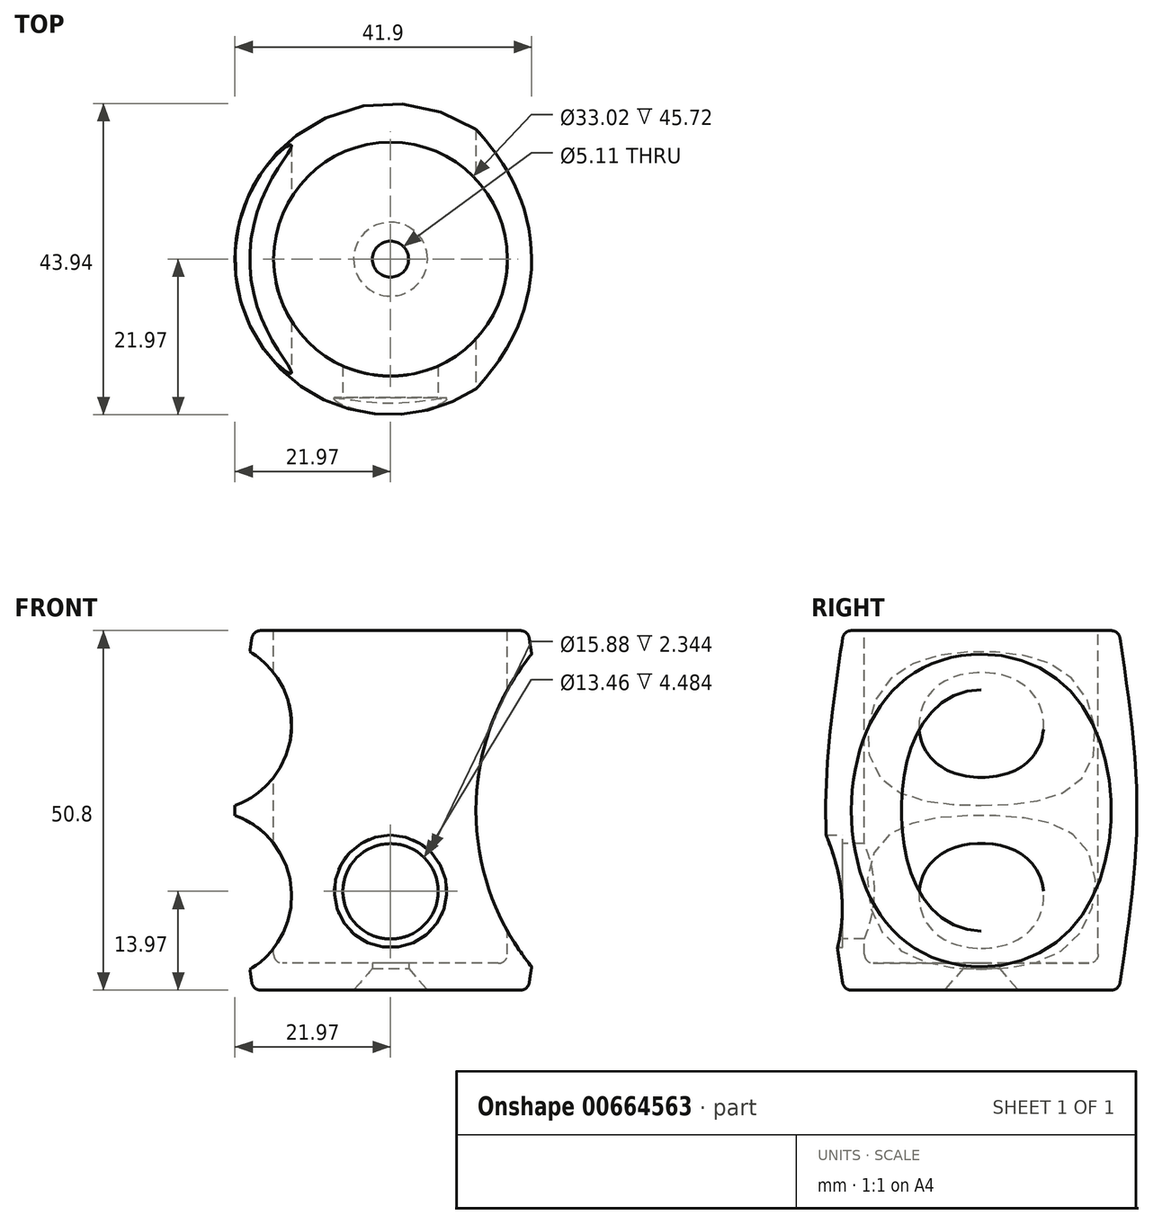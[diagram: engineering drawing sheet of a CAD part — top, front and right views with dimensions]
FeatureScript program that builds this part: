
annotation { "Feature Type Name" : "Feature", "Feature Type Description" : "" }
export const myFeature = defineFeature(function(context is Context, id is Id, definition is map)
    precondition{}
    {
        {
            var Q0;
            Q0=qCreatedBy(makeId("Front.planeOp"),FACE);
            var sketch = newSketch(context, id + "F0", { "sketchPlane" : qUnion([Q0])});
            skLineSegment(sketch, "E0.bottom", {"start": v(-18.34, 25.4) * mm, "end": v(-16.51, 25.4) * mm});
            skLineSegment(sketch, "E0.top", {"start": v(-18.34, -25.4) * mm, "end": v(0, -25.4) * mm});
            skPoint(sketch, "E0.middle", {"position": v(0, 0) * mm});
            skLineSegment(sketch, "E1", {"start": v(-19.43, 25.4) * mm, "end": v(-19.43, -24.78) * mm, "construction": true});
            skLineSegment(sketch, "E2", {"start": v(0, 25.4) * mm, "end": v(0, -21.59) * mm, "construction": true});
            skFitSpline(sketch, "E3", {"points": [v(-19.43, -25.4) * mm, v(-21.97, 0) * mm, v(-19.43, 25.4) * mm], "startDerivative": vector(-7.62, 50.8) * mm, "endDerivative": vector(7.62, 50.8) * mm});
            skArc(sketch, "E4.filletArc", {"start": v(-18.34, 25.4) * mm, "mid": v(-19.17, 25.1) * mm, "end": v(-19.6, 24.32) * mm});
            skArc(sketch, "E5.filletArc", {"start": v(-19.6, -24.32) * mm, "mid": v(-19.17, -25.1) * mm, "end": v(-18.34, -25.4) * mm});
            skLineSegment(sketch, "E6", {"start": v(0, -21.59) * mm, "end": v(-16.51, -21.59) * mm});
            skLineSegment(sketch, "E7", {"start": v(-16.51, -21.59) * mm, "end": v(-16.51, 25.4) * mm});
            skLineSegment(sketch, "E8", {"start": v(0, -21.59) * mm, "end": v(0, -25.4) * mm});
            skSolve(sketch);
        }
        {
            var Q0;
            Q0 = qSketchRegion(id + "F0", true);
            var Q1;
            Q1=sQuery(id+"F0.wireOp",EDGE,"E0.bottom");
            var Q2;
            Q2=sQuery(id+"F0.wireOp",EDGE,"E4.filletArc");
            var Q3;
            Q3=sQuery(id+"F0.wireOp",EDGE,"E3");
            var Q4;
            Q4=sQuery(id+"F0.wireOp",EDGE,"E5.filletArc");
            var Q5;
            Q5=sQuery(id+"F0.wireOp",EDGE,"E0.top");
            var Q6;
            Q6=sQuery(id+"F0.wireOp",EDGE,"E7");
            var Q7;
            Q7=sQuery(id+"F0.wireOp",EDGE,"E6");
            var Q8;
            Q8=sQuery(id+"F0.wireOp",EDGE,"E2");
            revolve(context, id + "F1", {"entities" : qUnion([Q0]), "surfaceEntities" : qUnion([Q1, Q2, Q3, Q4, Q5, Q6, Q7]), "axis" : qUnion([Q8]), "revolveType" : RevolveType.FULL});
        }
        {
            var Q0;
            Q0=qCreatedBy(makeId("Front.planeOp"),FACE);
            var sketch = newSketch(context, id + "F2", { "sketchPlane" : qUnion([Q0])});
            skCircle(sketch, "E9.MirrorC", {"center": v(47, 0) * mm, "radius": 34.93 * mm});
            skCircle(sketch, "E10.MirrorC", {"center": v(-26.04, 12.07) * mm, "radius": 12.07 * mm});
            skCircle(sketch, "E11.MirrorC", {"center": v(-26.04, -12.07) * mm, "radius": 12.07 * mm});
            skLineSegment(sketch, "E12", {"start": v(0, 0) * mm, "end": v(47, 0) * mm, "construction": true});
            skLineSegment(sketch, "E13", {"start": v(-26.04, 12.07) * mm, "end": v(-26.04, -12.07) * mm, "construction": true});
            skSolve(sketch);
        }
        {
            var Q0;
            Q0 = qSketchRegion(id + "F2", true);
            extrude(context, id + "F3", {"entities" : qUnion([Q0]), "operationType" : NewBodyOperationType.REMOVE, "endBound" : BoundingType.THROUGH_ALL, "oppositeDirection" : true, "depth" : 25.4 * mm, "offsetDistance" : 25.4 * mm, "hasSecondDirection" : true, "secondDirectionBound" : SecondDirectionBoundingType.THROUGH_ALL, "secondDirectionOppositeDirection" : false, "secondDirectionDepth" : 25.4 * mm});
        }
        {
            var Q0;
            Q0=qCreatedBy(makeId("Front.planeOp"),FACE);
            cPlane(context, id + "F4", {"entities" : qUnion([Q0]), "cplaneType" : CPlaneType.OFFSET, "offset" : 19.56 * mm, "width" : 152.4 * mm, "height" : 152.4 * mm});
        }
        {
            var Q0;
            Q0=qCreatedBy(id+"F4.planeOp",FACE);
            var sketch = newSketch(context, id + "F5", { "sketchPlane" : qUnion([Q0])});
            skCircle(sketch, "E14", {"center": v(0, -11.43) * mm, "radius": 7.94 * mm});
            skSolve(sketch);
        }
        {
            var Q0;
            Q0 = qSketchRegion(id + "F5", true);
            extrude(context, id + "F6", {"entities" : qUnion([Q0]), "operationType" : NewBodyOperationType.REMOVE, "endBound" : BoundingType.THROUGH_ALL, "depth" : 25.4 * mm, "offsetDistance" : 25.4 * mm});
        }
        {
            var Q0;
            Q0=sQuery(id+"F5.wireOp",VERTEX,"E14.center");
            var Q1;
            Q1=makeQuery(id+"F1.opRevolve","SWEPT_BODY",BODY,{"disambiguationData":[OSD([sQuery(id+"F0.wireOp",EDGE,"E0.bottom"),sQuery(id+"F0.wireOp",EDGE,"E0.top"),sQuery(id+"F0.wireOp",EDGE,"E3"),sQuery(id+"F0.wireOp",EDGE,"E4.filletArc"),sQuery(id+"F0.wireOp",EDGE,"E5.filletArc"),sQuery(id+"F0.wireOp",EDGE,"E6"),sQuery(id+"F0.wireOp",EDGE,"E7"),sQuery(id+"F0.wireOp",EDGE,"E8")])]});
            hole(context, id + "F7", {"style" : HoleStyle.SIMPLE, "endStyle" : HoleEndStyle.BLIND, "holeDiameter" : 13.46 * mm, "majorDiameter" : 12.7 * mm, "holeDepth" : 7.26 * mm, "isTappedThrough" : true, "tappedDepth" : 6.35 * mm, "tapClearance" : 1, "locations" : qUnion([Q0]), "scope" : qUnion([Q1])});
        }
        {
            var Q0;
            Q0=makeQuery(id+"F1.opRevolve","SWEPT_FACE",FACE,{"disambiguationData":[OSD([sQuery(id+"F0.wireOp",EDGE,"E0.top")])]});
            var sketch = newSketch(context, id + "F8", { "sketchPlane" : qUnion([Q0])});
            skPoint(sketch, "E15", {"position": v(0, 0) * mm});
            skSolve(sketch);
        }
        {
            var Q0;
            Q0=sQuery(id+"F8.wireOp",VERTEX,"E15");
            var Q1;
            Q1=makeQuery(id+"F1.opRevolve","SWEPT_BODY",BODY,{"disambiguationData":[OSD([sQuery(id+"F0.wireOp",EDGE,"E0.bottom"),sQuery(id+"F0.wireOp",EDGE,"E0.top"),sQuery(id+"F0.wireOp",EDGE,"E3"),sQuery(id+"F0.wireOp",EDGE,"E4.filletArc"),sQuery(id+"F0.wireOp",EDGE,"E5.filletArc"),sQuery(id+"F0.wireOp",EDGE,"E6"),sQuery(id+"F0.wireOp",EDGE,"E7"),sQuery(id+"F0.wireOp",EDGE,"E8")])]});
            hole(context, id + "F9", {"style" : HoleStyle.C_SINK, "endStyle" : HoleEndStyle.BLIND, "standardTappedOrClearance" : lookupTablePath({ "standard" : "ANSI", "fit" : "Normal (ASME)", "size" : "#10", "type" : "Clearance" }), "standardBlindInLast" : lookupTablePath({ "fit" : "Free", "standard" : "ANSI", "size" : "#10", "type" : "Clearance" }), "holeDiameter" : 5.1 * mm, "cSinkDiameter" : 10.44 * mm, "cSinkAngle" : 82 * degree, "majorDiameter" : 6.35 * mm, "holeDepth" : 7.95 * mm, "isTappedThrough" : true, "tappedDepth" : 6.35 * mm, "tapClearance" : 1, "locations" : qUnion([Q0]), "scope" : qUnion([Q1])});
        }
        {
            var Q0;
            Q0=makeQuery(id+"F1.opRevolve","SWEPT_EDGE",EDGE,{"disambiguationData":[OSD([sQuery(id+"F0.wireOp",EDGE,"E6"),sQuery(id+"F0.wireOp",EDGE,"E7")])]});
            fillet(context, id + "F10", {"entities" : qUnion([Q0]), "radius" : 1.27 * mm, "tangentPropagation" : true, "allowEdgeOverflow" : false});
        }
    });
